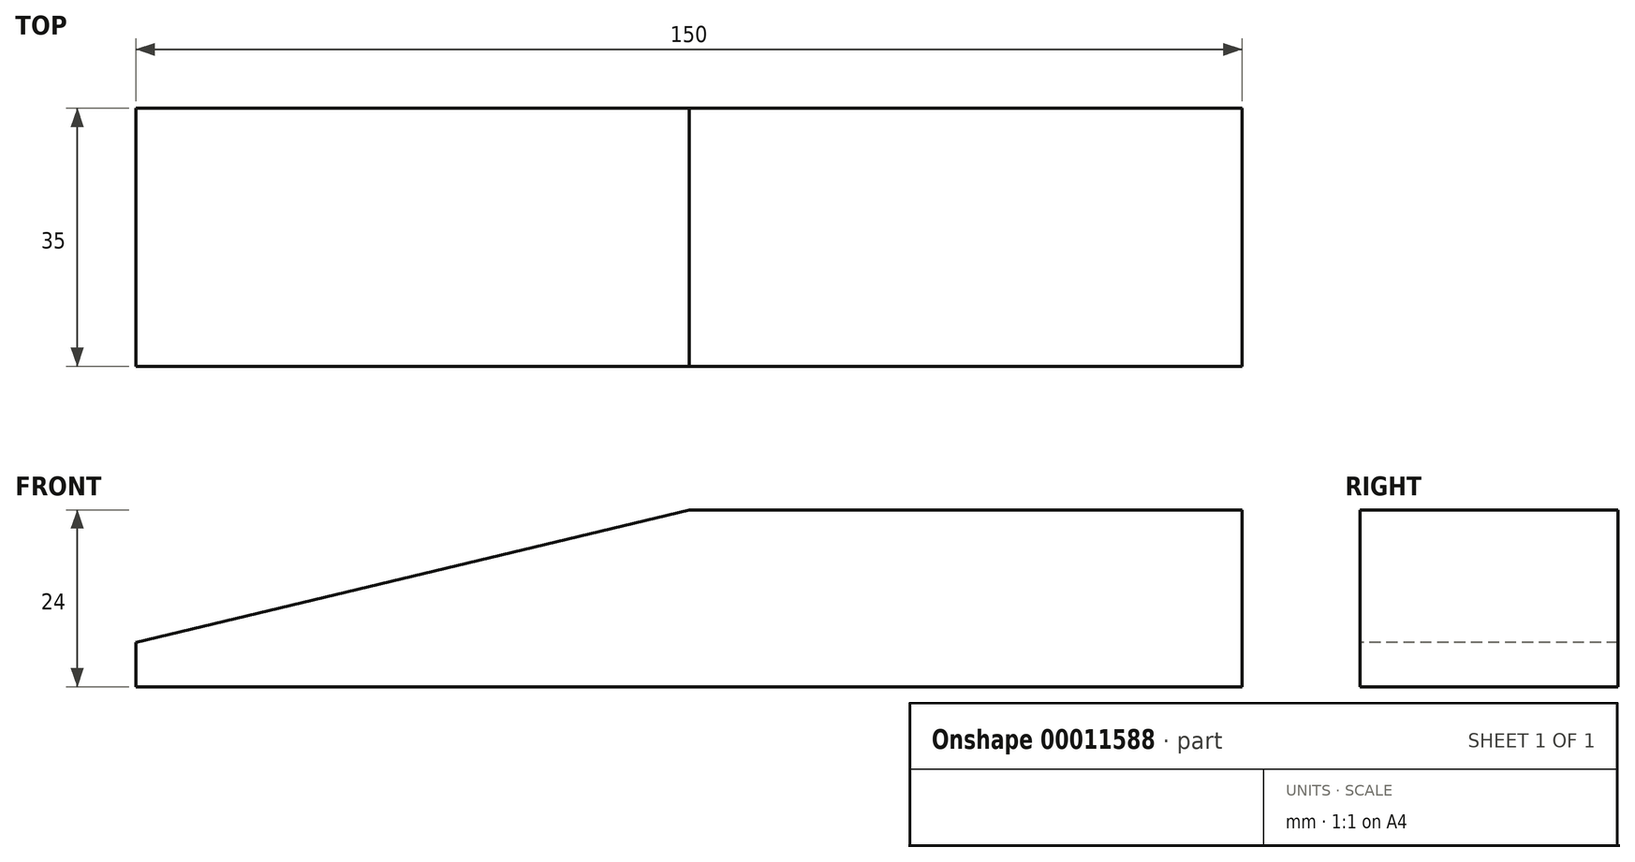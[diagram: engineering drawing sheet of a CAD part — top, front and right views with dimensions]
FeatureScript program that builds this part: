
annotation { "Feature Type Name" : "Feature", "Feature Type Description" : "" }
export const myFeature = defineFeature(function(context is Context, id is Id, definition is map)
    precondition{}
    {
        {
            var Q0;
            Q0=qCreatedBy(makeId("Top.planeOp"),FACE);
            var sketch = newSketch(context, id + "F0", { "sketchPlane" : qUnion([Q0])});
            skLineSegment(sketch, "E0.bottom", {"start": v(75, 17.5) * mm, "end": v(-75, 17.5) * mm});
            skLineSegment(sketch, "E0.top", {"start": v(75, -17.5) * mm, "end": v(-75, -17.5) * mm});
            skLineSegment(sketch, "E0.left", {"start": v(75, 17.5) * mm, "end": v(75, -17.5) * mm});
            skLineSegment(sketch, "E0.right", {"start": v(-75, 17.5) * mm, "end": v(-75, -17.5) * mm});
            skPoint(sketch, "E0.middle", {"position": v(0, 0) * mm});
            skSolve(sketch);
        }
        {
            var Q0;
            Q0=makeQuery(id+"F0.imprint","IMPRINT",FACE,{"disambiguationData":[TD([[makeQuery(id+"F0.imprint","IMPRINT",EDGE,{"derivedFrom":sQuery(id+"F0.wireOp",EDGE,"E0.bottom")}),1.0]])]});
            extrude(context, id + "F1", {"entities" : qUnion([Q0]), "depth" : 24 * mm});
        }
        {
            var Q0;
            Q0=makeQuery(id+"F1.opExtrude","SWEPT_FACE",FACE,{"disambiguationData":[OSD([sQuery(id+"F0.wireOp",EDGE,"E0.top")])]});
            var sketch = newSketch(context, id + "F2", { "sketchPlane" : qUnion([Q0])});
            skLineSegment(sketch, "E1", {"start": v(-82.08, 6) * mm, "end": v(18.6, 6) * mm, "construction": true});
            skLineSegment(sketch, "E2", {"start": v(0, 32.04) * mm, "end": v(0, -12.48) * mm, "construction": true});
            skLineSegment(sketch, "E3", {"start": v(-75, 6) * mm, "end": v(0, 24) * mm});
            skSolve(sketch);
        }
        {
            var Q0;
            {var subQ0=sQuery(id+"F2.wireOp",EDGE,"E3");Q0=makeQuery(id+"F2.imprint","IMPRINT",FACE,{"disambiguationData":[TD([[makeQuery(id+"F2.imprint","IMPRINT",EDGE,{"derivedFrom":subQ0}),1.0]])]});}
            extrude(context, id + "F3", {"entities" : qUnion([Q0]), "operationType" : NewBodyOperationType.REMOVE, "oppositeDirection" : true, "depth" : 35 * mm});
        }
    });
